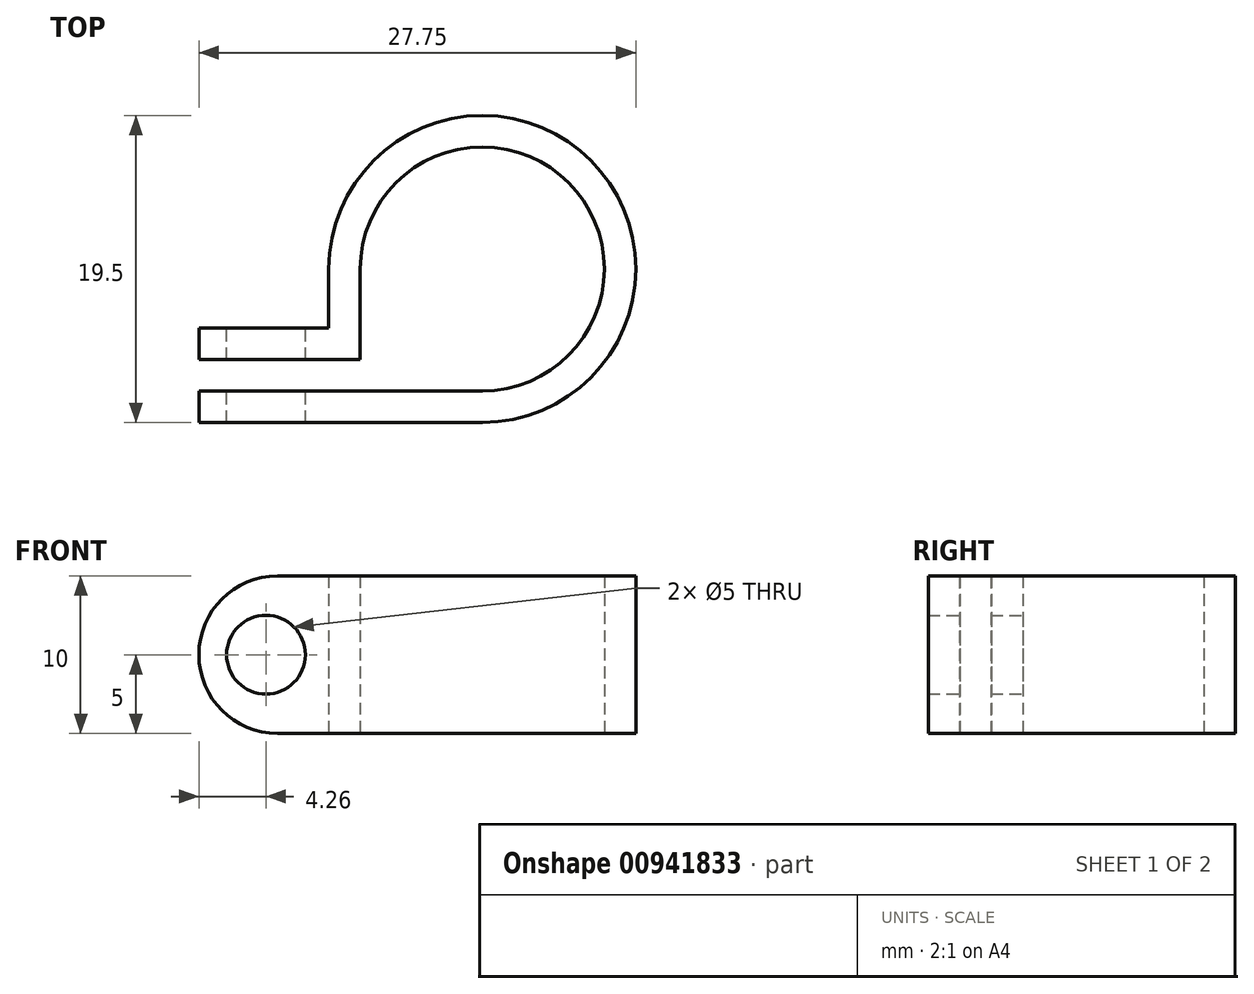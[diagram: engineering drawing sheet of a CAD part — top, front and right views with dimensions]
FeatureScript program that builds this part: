
annotation { "Feature Type Name" : "Feature", "Feature Type Description" : "" }
export const myFeature = defineFeature(function(context is Context, id is Id, definition is map)
    precondition{}
    {
        {
            var Q0;
            Q0=qCreatedBy(makeId("Top.planeOp"),FACE);
            var sketch = newSketch(context, id + "F0", { "sketchPlane" : qUnion([Q0])});
            skArc(sketch, "E0", {"start": v(0, -7.75) * mm, "mid": v(5.48, 5.48) * mm, "end": v(-7.75, 0) * mm});
            skLineSegment(sketch, "E1", {"start": v(0, -9.75) * mm, "end": v(-18, -9.75) * mm});
            skLineSegment(sketch, "E2", {"start": v(-18, -9.75) * mm, "end": v(-18, -7.75) * mm});
            skLineSegment(sketch, "E3", {"start": v(-18, -7.75) * mm, "end": v(0, -7.75) * mm});
            skLineSegment(sketch, "E4", {"start": v(-9.75, 0) * mm, "end": v(-9.75, -3.75) * mm});
            skLineSegment(sketch, "E5", {"start": v(-7.75, 0) * mm, "end": v(-7.75, -5.75) * mm});
            skArc(sketch, "E6.trimOffspring", {"start": v(0, -9.75) * mm, "mid": v(6.9, 6.9) * mm, "end": v(-9.75, 0) * mm});
            skLineSegment(sketch, "E7", {"start": v(-9.75, -3.75) * mm, "end": v(-18, -3.75) * mm});
            skLineSegment(sketch, "E8", {"start": v(-18, -3.75) * mm, "end": v(-18, -5.75) * mm});
            skLineSegment(sketch, "E9", {"start": v(-18, -5.75) * mm, "end": v(-7.75, -5.75) * mm});
            skSolve(sketch);
        }
        {
            var Q0;
            Q0=makeQuery(id+"F0.imprint","IMPRINT",FACE,{"disambiguationData":[TD([[makeQuery(id+"F0.imprint","IMPRINT",EDGE,{"derivedFrom":sQuery(id+"F0.wireOp",EDGE,"E0")}),-1.0]])]});
            extrude(context, id + "F1", {"entities" : qUnion([Q0]), "depth" : 10 * mm, "offsetDistance" : 25 * mm});
        }
        {
            var Q0;
            Q0=makeQuery(id+"F1.opExtrude","CAP_EDGE",EDGE,{"disambiguationData":[OSD([sQuery(id+"F0.wireOp",EDGE,"E8")])],"isStart":true});
            var Q1;
            Q1=makeQuery(id+"F1.opExtrude","CAP_EDGE",EDGE,{"disambiguationData":[OSD([sQuery(id+"F0.wireOp",EDGE,"E2")])],"isStart":true});
            var Q2;
            Q2=makeQuery(id+"F1.opExtrude","CAP_EDGE",EDGE,{"disambiguationData":[OSD([sQuery(id+"F0.wireOp",EDGE,"E2")])],"isStart":false});
            var Q3;
            Q3=makeQuery(id+"F1.opExtrude","CAP_EDGE",EDGE,{"disambiguationData":[OSD([sQuery(id+"F0.wireOp",EDGE,"E8")])],"isStart":false});
            fillet(context, id + "F2", {"entities" : qUnion([Q0, Q1, Q2, Q3]), "radius" : 5 * mm, "tangentPropagation" : true, "allowEdgeOverflow" : false});
        }
        {
            var Q0;
            Q0=makeQuery(id+"F1.opExtrude","SWEPT_FACE",FACE,{"disambiguationData":[OSD([sQuery(id+"F0.wireOp",EDGE,"E7")])]});
            var sketch = newSketch(context, id + "F3", { "sketchPlane" : qUnion([Q0])});
            skPoint(sketch, "E10", {"position": v(18, 5) * mm});
            skPoint(sketch, "E11", {"position": v(13.74, 5) * mm});
            skSolve(sketch);
        }
        {
            var Q0;
            Q0=sQuery(id+"F3.wireOp",VERTEX,"E11");
            var Q1;
            Q1=makeQuery(id+"F1.opExtrude","SWEPT_BODY",BODY,{"disambiguationData":[OSD([sQuery(id+"F0.wireOp",EDGE,"E0"),sQuery(id+"F0.wireOp",EDGE,"E1"),sQuery(id+"F0.wireOp",EDGE,"E2"),sQuery(id+"F0.wireOp",EDGE,"E3"),sQuery(id+"F0.wireOp",EDGE,"E4"),sQuery(id+"F0.wireOp",EDGE,"E5"),sQuery(id+"F0.wireOp",EDGE,"E6.trimOffspring"),sQuery(id+"F0.wireOp",EDGE,"E7"),sQuery(id+"F0.wireOp",EDGE,"E8"),sQuery(id+"F0.wireOp",EDGE,"E9")])]});
            hole(context, id + "F4", {"style" : HoleStyle.SIMPLE, "endStyle" : HoleEndStyle.THROUGH, "holeDiameter" : 5 * mm, "majorDiameter" : 5 * mm, "isTappedThrough" : true, "tappedDepth" : 12 * mm, "tapClearance" : 3, "locations" : qUnion([Q0]), "scope" : qUnion([Q1])});
        }
    });
